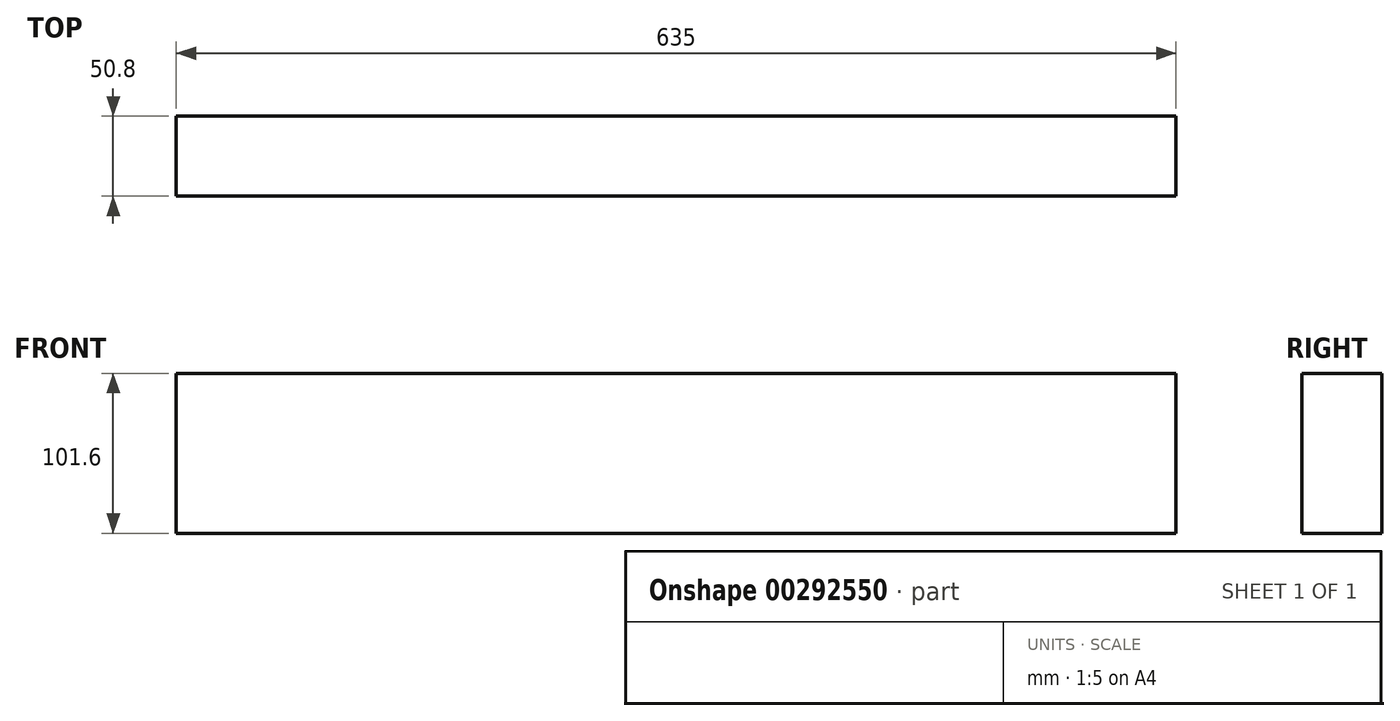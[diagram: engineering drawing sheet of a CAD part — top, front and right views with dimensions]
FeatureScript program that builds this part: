
annotation { "Feature Type Name" : "Feature", "Feature Type Description" : "" }
export const myFeature = defineFeature(function(context is Context, id is Id, definition is map)
    precondition{}
    {
        {
            var Q0;
            Q0=qCreatedBy(makeId("Top.planeOp"),FACE);
            var sketch = newSketch(context, id + "F0", { "sketchPlane" : qUnion([Q0])});
            skLineSegment(sketch, "E0.bottom", {"start": v(0, 0) * mm, "end": v(635, 0) * mm});
            skLineSegment(sketch, "E0.top", {"start": v(0, 50.8) * mm, "end": v(635, 50.8) * mm});
            skLineSegment(sketch, "E0.left", {"start": v(0, 0) * mm, "end": v(0, 50.8) * mm});
            skLineSegment(sketch, "E0.right", {"start": v(635, 0) * mm, "end": v(635, 50.8) * mm});
            skSolve(sketch);
        }
        {
            var Q0;
            Q0=makeQuery(id+"F0.imprint","IMPRINT",FACE,{"disambiguationData":[TD([[makeQuery(id+"F0.imprint","IMPRINT",EDGE,{"derivedFrom":sQuery(id+"F0.wireOp",EDGE,"E0.bottom")}),1.0]])]});
            extrude(context, id + "F1", {"entities" : qUnion([Q0]), "depth" : 101.6 * mm, "offsetDistance" : 25.4 * mm});
        }
    });
